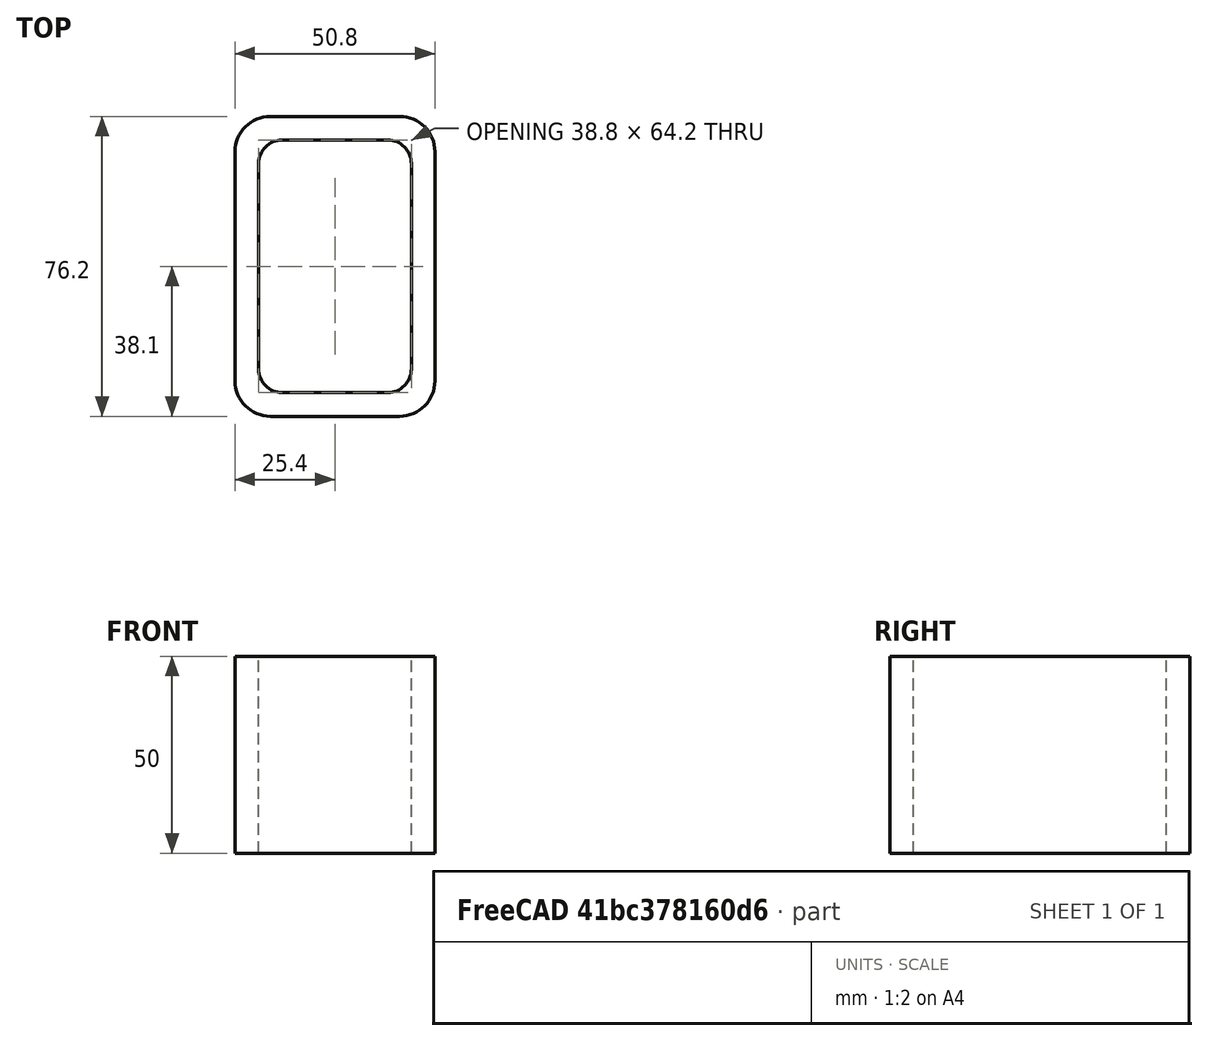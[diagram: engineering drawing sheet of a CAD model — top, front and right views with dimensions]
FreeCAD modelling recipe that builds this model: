
FCSTD DOCUMENT  (FreeCAD 0.15R4671 (Git))
Label: Rectangular hollow section 76.2 x50.8 x6 EN10219 S235JRH
License: All rights reserved
LicenseURL: http://en.wikipedia.org/wiki/All_rights_reserved
objects: Sketcher::SketchObject×1, Part::Extrusion×1
note: 2 computed .brp shape members not serialized (recipe doc carries the construction recipe); baked Part::Feature solids carry a one-line shape summary decoded from their .brp

FEATURE [Sketcher::SketchObject] Sketch
  sketch-geometry (16):
    g0: LineSegment StartX=-13.4 StartY=32.1 StartZ=0 EndX=13.4 EndY=32.1 EndZ=0
    g1: LineSegment StartX=19.4 StartY=26.1 StartZ=0 EndX=19.4 EndY=-26.1 EndZ=0
    g2: LineSegment StartX=13.4 StartY=-32.1 StartZ=0 EndX=-13.4 EndY=-32.1 EndZ=0
    g3: LineSegment StartX=-19.4 StartY=-26.1 StartZ=0 EndX=-19.4 EndY=26.1 EndZ=0
    g4: LineSegment StartX=-16.4 StartY=38.1 StartZ=0 EndX=16.4 EndY=38.1 EndZ=0
    g5: LineSegment StartX=25.4 StartY=29.1 StartZ=0 EndX=25.4 EndY=-29.1 EndZ=0
    g6: LineSegment StartX=16.4 StartY=-38.1 StartZ=0 EndX=-16.4 EndY=-38.1 EndZ=0
    g7: LineSegment StartX=-25.4 StartY=-29.1 StartZ=0 EndX=-25.4 EndY=29.1 EndZ=0
    g8: ArcOfCircle CenterX=-13.4 CenterY=26.1 CenterZ=0 NormalX=0 NormalY=0 NormalZ=1 Radius=6 StartAngle=1.5708 EndAngle=3.14159
    g9: ArcOfCircle CenterX=13.4 CenterY=26.1 CenterZ=0 NormalX=0 NormalY=0 NormalZ=1 Radius=6 StartAngle=0 EndAngle=1.5708
    g10: ArcOfCircle CenterX=13.4 CenterY=-26.1 CenterZ=0 NormalX=0 NormalY=0 NormalZ=1 Radius=6 StartAngle=4.71239 EndAngle=6.28319
    g11: ArcOfCircle CenterX=-13.4 CenterY=-26.1 CenterZ=0 NormalX=0 NormalY=0 NormalZ=1 Radius=6 StartAngle=3.14159 EndAngle=4.71239
    g12: ArcOfCircle CenterX=16.4 CenterY=29.1 CenterZ=0 NormalX=0 NormalY=0 NormalZ=1 Radius=9 StartAngle=0 EndAngle=1.5708
    g13: ArcOfCircle CenterX=16.4 CenterY=-29.1 CenterZ=0 NormalX=0 NormalY=0 NormalZ=1 Radius=9 StartAngle=4.71239 EndAngle=6.28319
    g14: ArcOfCircle CenterX=-16.4 CenterY=-29.1 CenterZ=0 NormalX=0 NormalY=0 NormalZ=1 Radius=9 StartAngle=3.14159 EndAngle=4.71239
    g15: ArcOfCircle CenterX=-16.4 CenterY=29.1 CenterZ=0 NormalX=0 NormalY=0 NormalZ=1 Radius=9 StartAngle=1.5708 EndAngle=3.14159
  constraints (36):
    c: Horizontal(g2)
    c: Vertical(g3)
    c: Horizontal(g6)
    c: Vertical(g7)
    c: Tangent(g3,g8) = 1.5708
    c: Tangent(g0,g8) = 1.5708
    c: Tangent(g0,g9) = 1.5708
    c: Tangent(g1,g9) = 1.5708
    c: Tangent(g1,g10) = 1.5708
    c: Tangent(g2,g10) = 1.5708
    c: Tangent(g2,g11) = 1.5708
    c: Tangent(g3,g11) = 1.5708
    c: Tangent(g4,g12) = 1.5708
    c: Tangent(g5,g12) = 1.5708
    c: Tangent(g5,g13) = 1.5708
    c: Tangent(g6,g13) = 1.5708
    c: Tangent(g6,g14) = 1.5708
    c: Tangent(g7,g14) = 1.5708
    c: Tangent(g7,g15) = 1.5708
    c: Tangent(g4,g15) = 1.5708
    c: Equal(g9,g8)
    c: Equal(g9,g11)
    c: Equal(g9,g10)
    c: Equal(g12,g15)
    c: Equal(g12,g14)
    c: Equal(g12,g13)
    c: Symmetric(g4,g6,g-1)
    c: Symmetric(g7,g5,g-2)
    c: DistanceY(g4,g6) = -76.2
    c: DistanceX(g7,g5) = 50.8
    c: Symmetric(g3,g1,g-2)
    c: Symmetric(g0,g2,g-1)
    c: DistanceY(g0,g4) = 6
    c: DistanceX(g5,g1) = -6
    c: Radius(g9) = 6
    c: Radius(g12) = 9
FEATURE [Part::Extrusion] Extrude  label="Rectangular hollow section 76.2 x50.8 x6 EN10219 S235JRH"
  Base = -> Sketch
  Dir = (0,0,50)
  Solid = true
